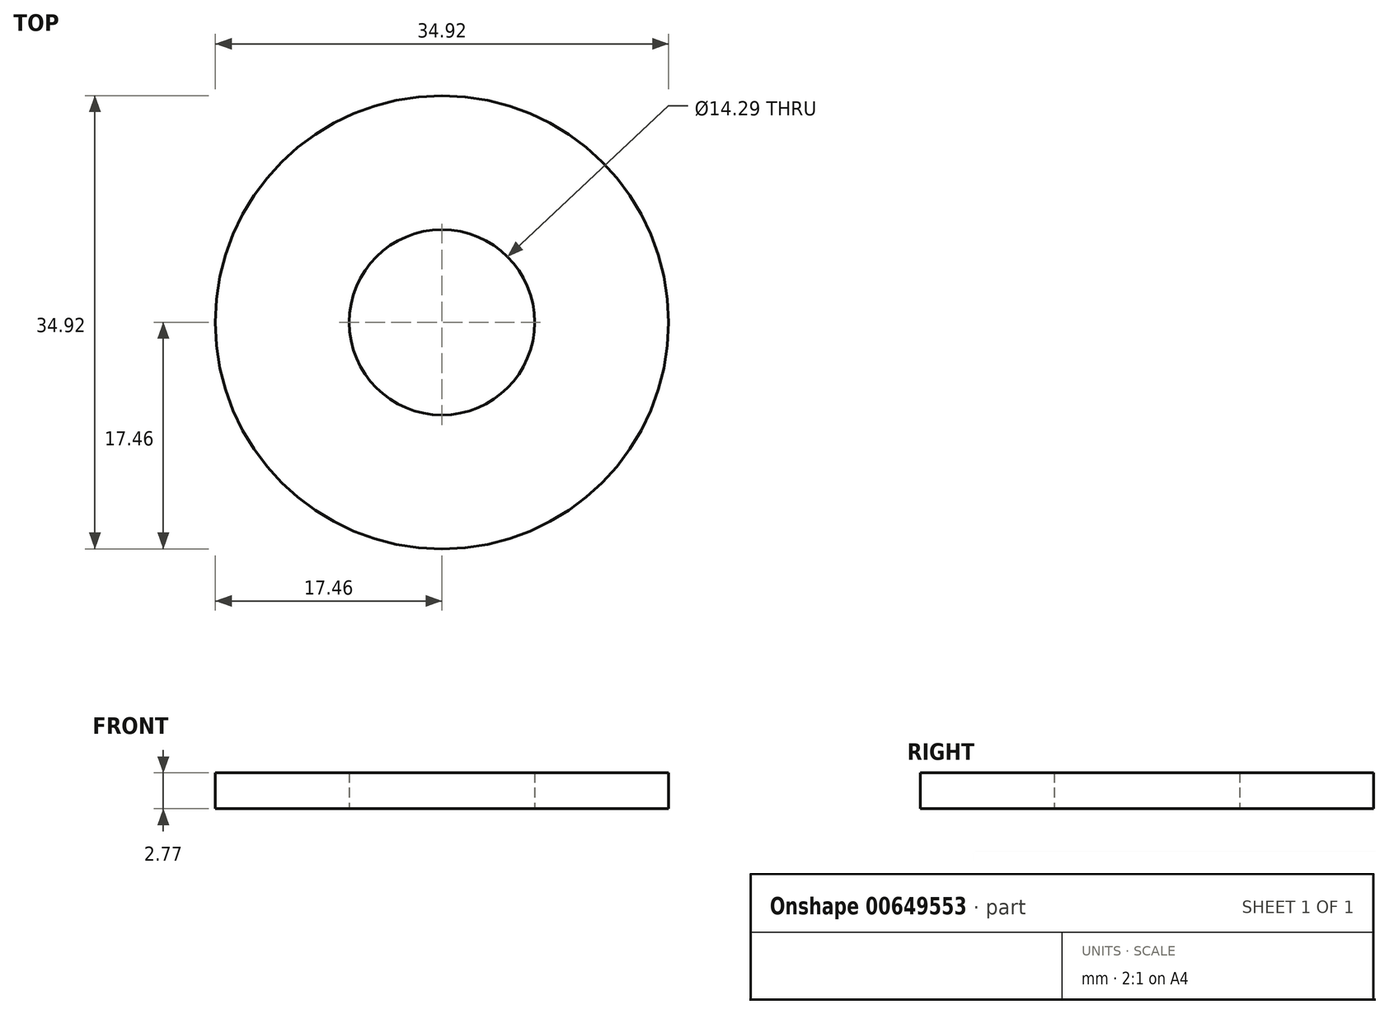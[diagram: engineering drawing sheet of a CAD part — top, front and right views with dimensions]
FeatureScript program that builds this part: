
annotation { "Feature Type Name" : "Feature", "Feature Type Description" : "" }
export const myFeature = defineFeature(function(context is Context, id is Id, definition is map)
    precondition{}
    {
        {
            var Q0;
            Q0=qCreatedBy(makeId("Top.planeOp"), FACE);
            var sketch = newSketch(context, id + "F0", { "sketchPlane" : qUnion([Q0])});
            skCircle(sketch, "E0", {"center": v(0, 0) * mm, "radius": 7.14 * mm});
            skCircle(sketch, "E1", {"center": v(0, 0) * mm, "radius": 17.46 * mm});
            skSolve(sketch);
        }
        {
            var Q0;
            Q0 = qSketchRegion(id + "F0", true);
            extrude(context, id + "F1", {"entities" : qUnion([Q0]), "depth" : 2.77 * mm, "offsetDistance" : 25.4 * mm});
        }
    });
